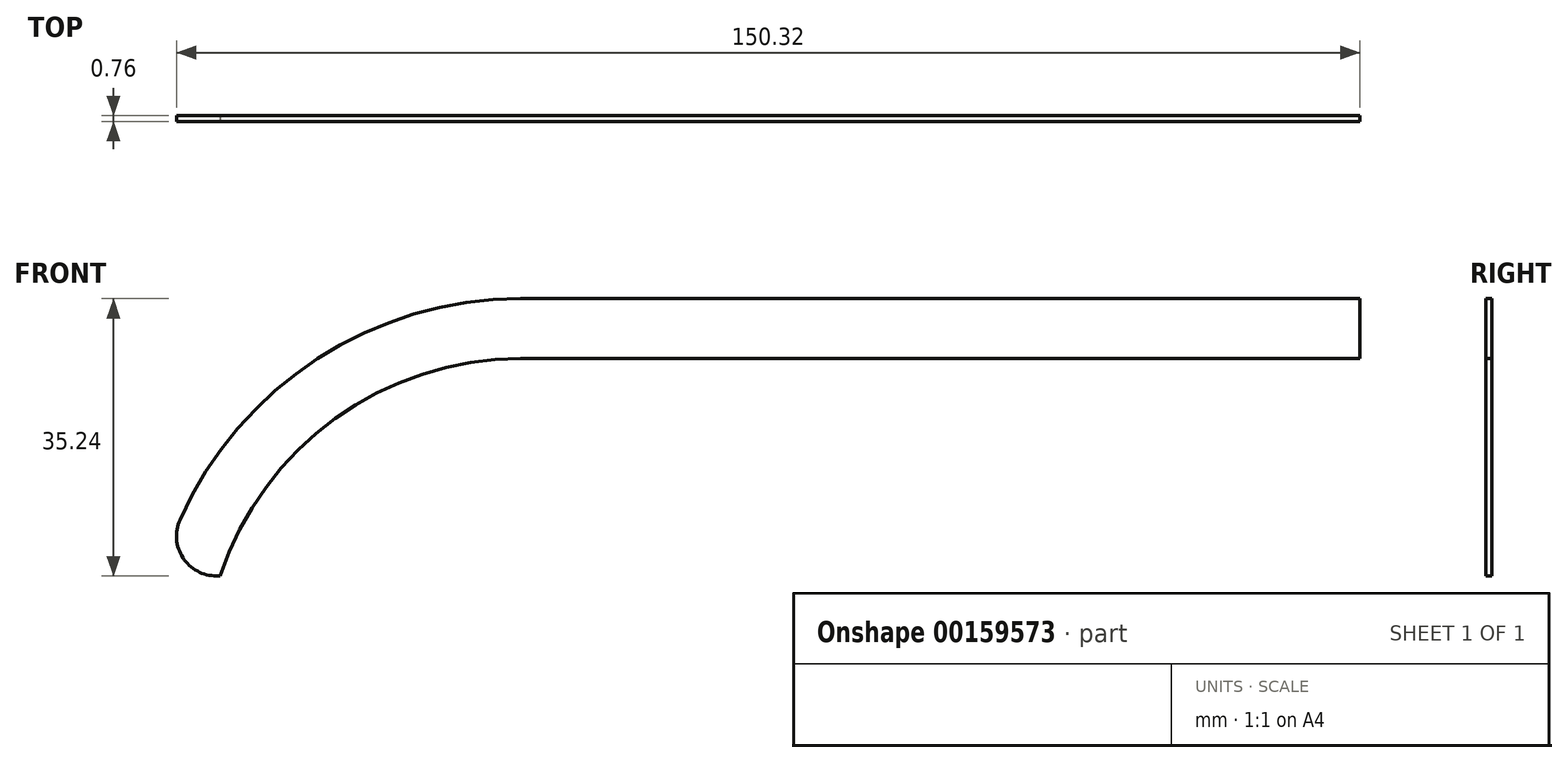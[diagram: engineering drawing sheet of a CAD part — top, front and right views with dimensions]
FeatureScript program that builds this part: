
annotation { "Feature Type Name" : "Feature", "Feature Type Description" : "" }
export const myFeature = defineFeature(function(context is Context, id is Id, definition is map)
    precondition{}
    {
        {
            var Q0;
            Q0=qCreatedBy(makeId("Front.planeOp"),FACE);
            var sketch = newSketch(context, id + "F0", { "sketchPlane" : qUnion([Q0])});
            skLineSegment(sketch, "E0", {"start": v(75.25, 0) * mm, "end": v(-31.34, 0) * mm});
            skArc(sketch, "E1", {"start": v(-31.34, 0) * mm, "mid": v(-60.24, -9.83) * mm, "end": v(-77.15, -35.24) * mm});
            skLineSegment(sketch, "E2", {"start": v(-31.34, -7.62) * mm, "end": v(75.25, -7.62) * mm});
            skLineSegment(sketch, "E3", {"start": v(75.25, -7.62) * mm, "end": v(75.25, 0) * mm});
            skArc(sketch, "E4", {"start": v(-31.34, -7.62) * mm, "mid": v(-54.9, -15.25) * mm, "end": v(-69.53, -35.24) * mm});
            skLineSegment(sketch, "E5", {"start": v(-77.15, -35.24) * mm, "end": v(-69.53, -35.24) * mm});
            skSolve(sketch);
        }
        {
            var Q0;
            Q0=makeQuery(id+"F0.imprint","IMPRINT",FACE,{"disambiguationData":[TD([[makeQuery(id+"F0.imprint","IMPRINT",EDGE,{"derivedFrom":sQuery(id+"F0.wireOp",EDGE,"E0")}),1.0]])]});
            extrude(context, id + "F1", {"entities" : qUnion([Q0]), "oppositeDirection" : true, "depth" : 0.76 * mm});
        }
        {
            var Q0;
            Q0=makeQuery(id+"F1.opExtrude","SWEPT_EDGE",EDGE,{"disambiguationData":[OSD([sQuery(id+"F0.wireOp",EDGE,"E1"),sQuery(id+"F0.wireOp",EDGE,"E5")])]});
            fillet(context, id + "F2", {"entities" : qUnion([Q0]), "radius" : 5.08 * mm, "tangentPropagation" : true, "allowEdgeOverflow" : false});
        }
    });
